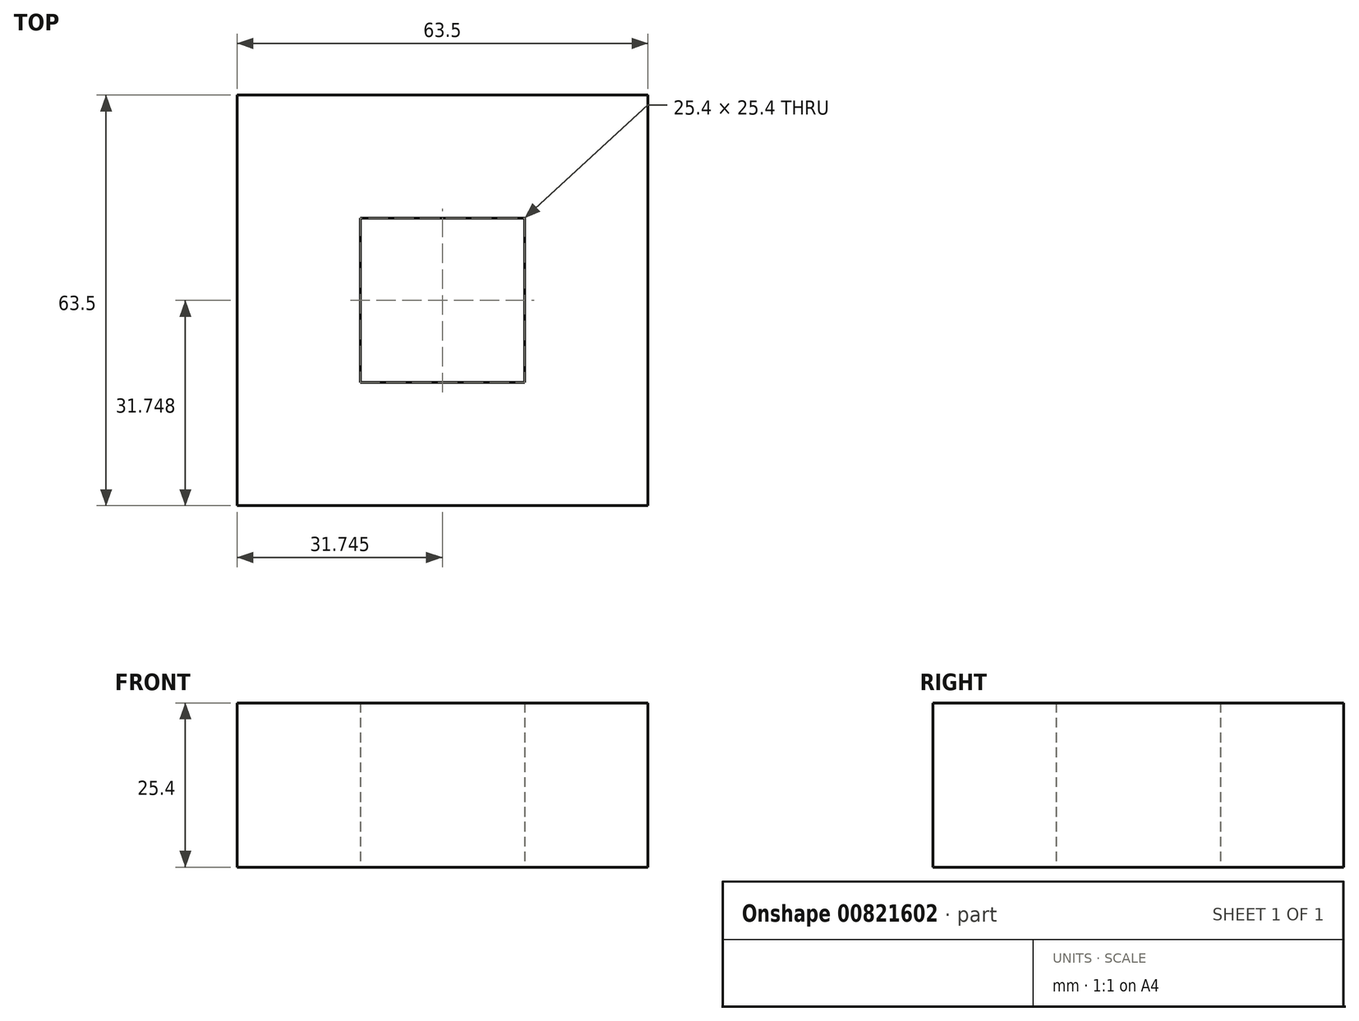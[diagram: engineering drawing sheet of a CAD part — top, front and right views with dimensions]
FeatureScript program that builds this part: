
annotation { "Feature Type Name" : "Feature", "Feature Type Description" : "" }
export const myFeature = defineFeature(function(context is Context, id is Id, definition is map)
    precondition{}
    {
        {
            var Q0;
            Q0=qCreatedBy(makeId("Top.planeOp"),FACE);
            var sketch = newSketch(context, id + "F0", { "sketchPlane" : qUnion([Q0])});
            skLineSegment(sketch, "E0", {"start": v(-38.81, 26.23) * mm, "end": v(-38.81, -37.27) * mm});
            skLineSegment(sketch, "E1", {"start": v(-38.81, -37.27) * mm, "end": v(24.69, -37.27) * mm});
            skLineSegment(sketch, "E2", {"start": v(24.69, -37.27) * mm, "end": v(24.69, 26.23) * mm});
            skLineSegment(sketch, "E3", {"start": v(24.69, 26.23) * mm, "end": v(-38.81, 26.23) * mm});
            skLineSegment(sketch, "E4.bottom", {"start": v(-19.76, 7.18) * mm, "end": v(5.64, 7.18) * mm});
            skLineSegment(sketch, "E4.top", {"start": v(-19.76, -18.22) * mm, "end": v(5.64, -18.22) * mm});
            skLineSegment(sketch, "E4.left", {"start": v(-19.76, 7.18) * mm, "end": v(-19.76, -18.22) * mm});
            skLineSegment(sketch, "E4.right", {"start": v(5.64, 7.18) * mm, "end": v(5.64, -18.22) * mm});
            skSolve(sketch);
        }
        {
            var Q0;
            Q0=makeQuery(id+"F0.imprint","IMPRINT",FACE,{"disambiguationData":[TD([[makeQuery(id+"F0.imprint","IMPRINT",EDGE,{"derivedFrom":sQuery(id+"F0.wireOp",EDGE,"E0")}),1.0]])]});
            extrude(context, id + "F1", {"entities" : qUnion([Q0]), "depth" : 25.4 * mm, "offsetDistance" : 25.4 * mm});
        }
    });
